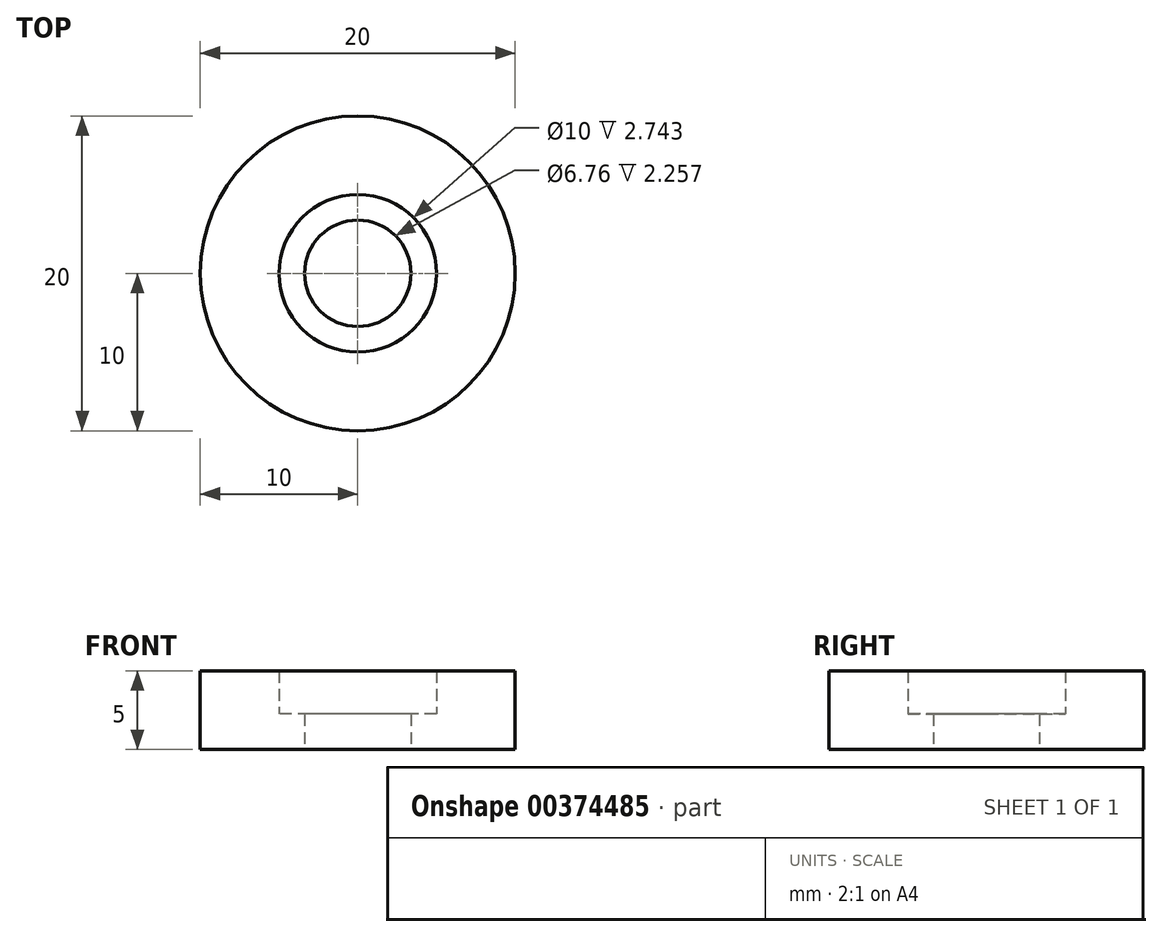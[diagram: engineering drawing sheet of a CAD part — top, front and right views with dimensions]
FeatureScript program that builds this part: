
annotation { "Feature Type Name" : "Feature", "Feature Type Description" : "" }
export const myFeature = defineFeature(function(context is Context, id is Id, definition is map)
    precondition{}
    {
        {
            var Q0;
            Q0=qCreatedBy(makeId("Top.planeOp"),FACE);
            var sketch = newSketch(context, id + "F0", { "sketchPlane" : qUnion([Q0])});
            skCircle(sketch, "E0", {"center": v(0, 0) * mm, "radius": 5 * mm});
            skCircle(sketch, "E1.0", {"center": v(0, 0) * mm, "radius": 10 * mm});
            skSolve(sketch);
        }
        {
            var Q0;
            Q0=makeQuery(id+"F0.imprint","IMPRINT",FACE,{"disambiguationData":[TD([[makeQuery(id+"F0.imprint","IMPRINT",EDGE,{"derivedFrom":sQuery(id+"F0.wireOp",EDGE,"E0")}),-1.0]])]});
            extrude(context, id + "F1", {"entities" : qUnion([Q0]), "depth" : 5 * mm});
        }
        {
            var Q0;
            Q0=qCreatedBy(makeId("Top.planeOp"),FACE);
            var sketch = newSketch(context, id + "F2", { "sketchPlane" : qUnion([Q0])});
            skCircle(sketch, "E2", {"center": v(0, 0) * mm, "radius": 3.38 * mm});
            skCircle(sketch, "E3.0", {"center": v(0, 0) * mm, "radius": 7.3 * mm});
            skSolve(sketch);
        }
        {
            var Q0;
            Q0 = qSketchRegion(id + "F2", true);
            extrude(context, id + "F3", {"entities" : qUnion([Q0]), "operationType" : NewBodyOperationType.ADD, "depth" : 2.26 * mm});
        }
    });
